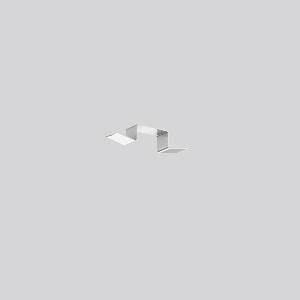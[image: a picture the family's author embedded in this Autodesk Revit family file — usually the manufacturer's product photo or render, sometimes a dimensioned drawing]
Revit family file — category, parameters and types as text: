
# Revit family: linedo_fixierklammer_982751_000_badc
name_source: partatom
category: Lighting Fixtures
units: mm (PartAtom-declared; Revit-internal decimal feet)

## family parameters
Cut with Voids When Loaded = No
Host = Face
Light Source = No
Part Type = Normal
Room Calculation Point = No
Round Connector Dimension = Use Diameter
Shared = No

## types (1)
- LINEDO Fixierklammer
    Apparent Load = 0 VA
    Default Elevation = 1800 mm
    Description = Fixing clamp. Spring steel, blank. For guiding external cables on top of the continuous line luminaire module.
Colour: stainless steel
Length: 10 mm
Width: 51 mm
Height: 10 mm
Weight: 2,6 g
Type of Installation: Recessed mounting, Surface mounting
    Height = 10 mm  [stored 0.0328084 ft]
    Lamp = 0 x
    Length = 10 mm  [stored 0.0328084 ft]
    Luminous efficacy = 0 lm/W
    Manufacturer = RZB
    ModVariant = No
    Model = 982751.000
    Mounting Place = Ceiling
    Mounting Type = Surface mounted
    Number of Poles = 1
    OnlyDefault = Yes
    Power Factor = 1
    Product Name = LINEDO Fixierklammer
    Product group = Surface mounted continuous line luminaire system
    ProductGroupID = 310
    Protection Class = Protection class
    Protection Degree = Degree of protection
    RLX_Detail_Level = 1
    RLX_Emergency_Light_Flux = 0 lm
    RLX_Emergency_Type = 0
    RLX_Emergency_Type_DB = No
    RlxData = <blob elided: 5413 chars, md5=516f9743>
    Standby Power = 0 W
    System Light Flux = 0 lm
    System Power = 0 W
    Type Comments = Product without accessories
    Type Image = 982751.000.jpg
    URL = http://relux.com
    VarID = ---
    Voltage = 0 V
    Weight = 0.00 kg
    Width = 51 mm

note: [stored X ft] marks values corroborated as IEEE doubles in the binary element streams (Revit-internal decimal feet)

## geometry (parser evidence)
native form markers: Blend x2, Sweep x9
no freeform markers — native parametric forms only
